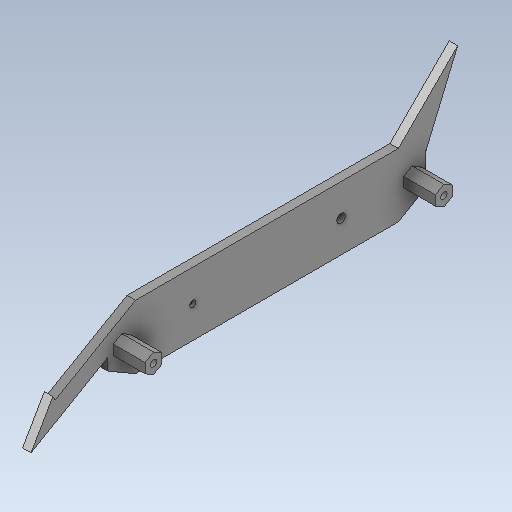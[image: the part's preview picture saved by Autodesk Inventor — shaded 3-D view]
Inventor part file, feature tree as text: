
AUTODESK INVENTOR PART (.ipt)
format: ipt  version: 2020 (Build 240168000, 168)  size: 176,128 bytes
history: native  units: in
note: dims shown in document units (in); Inventor stores cm internally (conversion verified against a paired STEP export)
features: other x3, extrude x2, sketch x2
ambient origin geometry x8: Origin, YZ Plane, XZ Plane, XY Plane, X Axis, Y Axis, Z Axis, Center Point
bodies: Solid1 (feature_tree)
feature tree (7):
  other  "HexWheelGuard.ipt"
  extrude  "Extrusion1"  TaperAngle=0.0deg  [1 undecoded]
  extrude  "Extrusion2"  Depth=0.5906in
  other  "Solid1::HexWheelGuard.ipt"
  other  "TaggingFeature1"
  sketch  "Sketch1"  dims[d0=0.3937in d6=0.0in d7=0.0in]
  sketch  "Sketch2"  dims[d9=0.315in d10=1.4843in d11=60.0deg d12=0.0787in d13=0.3937in d14=0.0in d20=0.3937in d21=0.5906in d22=1.1024in]
note: 1 required parameter value undecoded (feature->parameter linkage not recoverable at this tier; creation-order binding heuristic only, values carry confidence <= 0.55)
